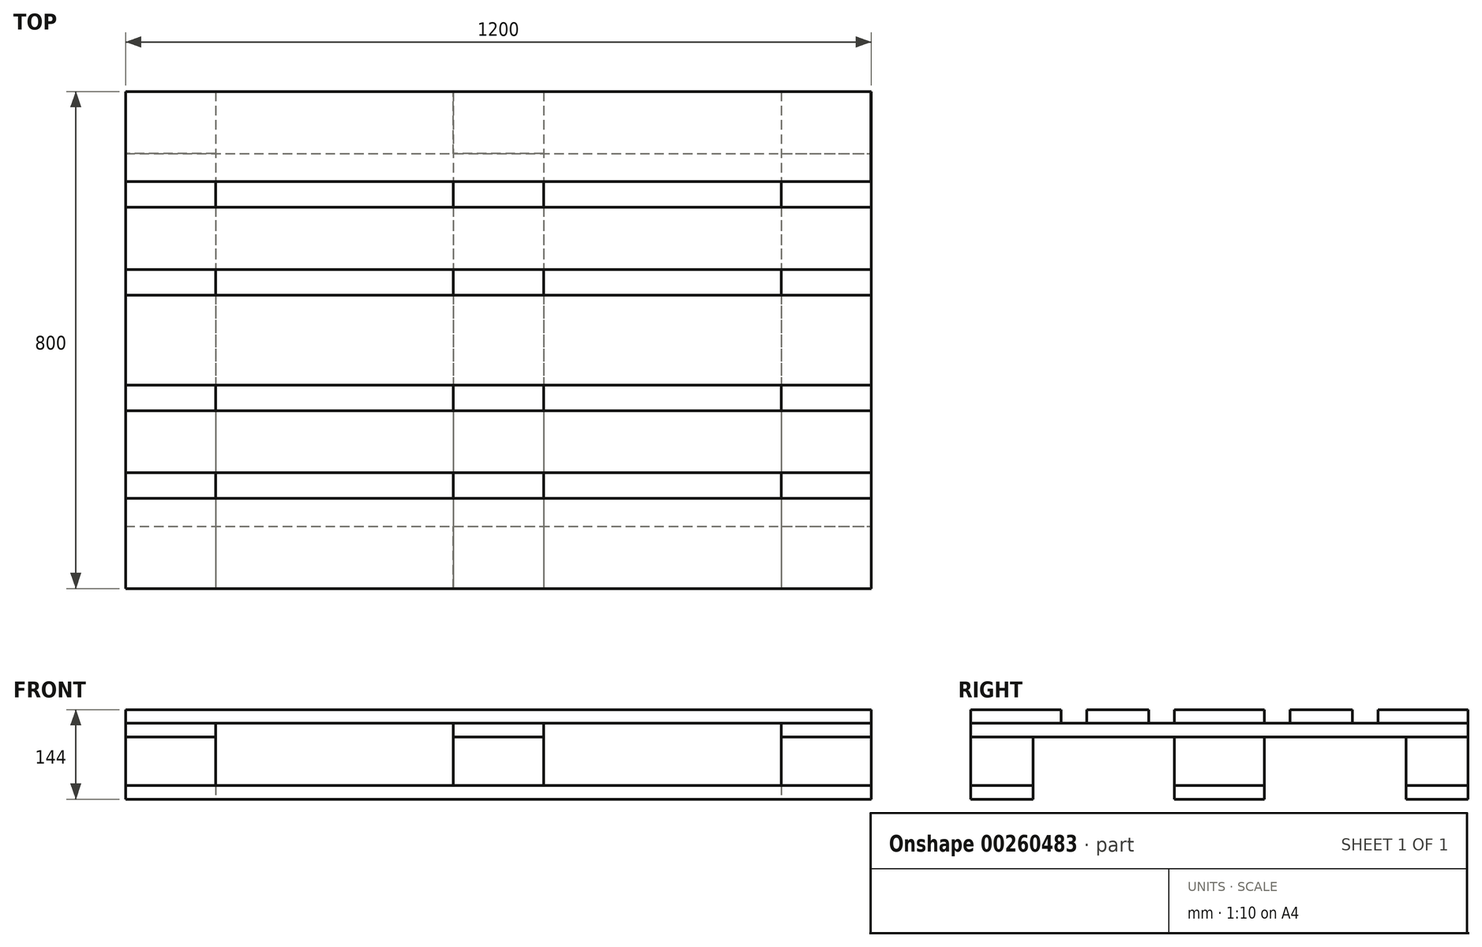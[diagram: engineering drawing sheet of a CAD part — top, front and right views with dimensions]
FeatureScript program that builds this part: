
annotation { "Feature Type Name" : "Feature", "Feature Type Description" : "" }
export const myFeature = defineFeature(function(context is Context, id is Id, definition is map)
    precondition{}
    {
        {
            var Q0;
            Q0=qCreatedBy(makeId("Top.planeOp"),FACE);
            var sketch = newSketch(context, id + "F0", { "sketchPlane" : qUnion([Q0])});
            skLineSegment(sketch, "E0.bottom", {"start": v(0, 800) * mm, "end": v(1200, 800) * mm});
            skLineSegment(sketch, "E0.top", {"start": v(0, 700) * mm, "end": v(1200, 700) * mm});
            skLineSegment(sketch, "E0.left", {"start": v(0, 800) * mm, "end": v(0, 700) * mm});
            skLineSegment(sketch, "E0.right", {"start": v(1200, 800) * mm, "end": v(1200, 700) * mm});
            skLineSegment(sketch, "E1.bottom", {"start": v(0, 100) * mm, "end": v(1200, 100) * mm});
            skLineSegment(sketch, "E1.top", {"start": v(0, 0) * mm, "end": v(1200, 0) * mm});
            skLineSegment(sketch, "E1.left", {"start": v(0, 100) * mm, "end": v(0, 0) * mm});
            skLineSegment(sketch, "E1.right", {"start": v(1200, 100) * mm, "end": v(1200, 0) * mm});
            skLineSegment(sketch, "E2.bottom", {"start": v(0, 472.5) * mm, "end": v(145, 472.5) * mm});
            skLineSegment(sketch, "E2.top", {"start": v(0, 327.5) * mm, "end": v(145, 327.5) * mm});
            skLineSegment(sketch, "E2.left", {"start": v(0, 472.5) * mm, "end": v(0, 327.5) * mm});
            skLineSegment(sketch, "E2.right", {"start": v(145, 472.5) * mm, "end": v(145, 327.5) * mm});
            skLineSegment(sketch, "E3.bottom", {"start": v(1055, 472.5) * mm, "end": v(1200, 472.5) * mm});
            skLineSegment(sketch, "E3.top", {"start": v(1055, 327.5) * mm, "end": v(1200, 327.5) * mm});
            skLineSegment(sketch, "E3.left", {"start": v(1055, 472.5) * mm, "end": v(1055, 327.5) * mm});
            skLineSegment(sketch, "E3.right", {"start": v(1200, 472.5) * mm, "end": v(1200, 327.5) * mm});
            skSolve(sketch);
        }
        {
            var Q0;
            Q0 = qSketchRegion(id + "F0", true);
            extrude(context, id + "F1", {"entities" : qUnion([Q0]), "depth" : 22 * mm});
        }
        {
            var Q0;
            Q0=makeQuery(id+"F1.opExtrude","CAP_FACE",FACE,{"disambiguationData":[OSD([sQuery(id+"F0.wireOp",EDGE,"E1.bottom"),sQuery(id+"F0.wireOp",EDGE,"E1.top"),sQuery(id+"F0.wireOp",EDGE,"E1.left"),sQuery(id+"F0.wireOp",EDGE,"E1.right")])],"isStart":false});
            var sketch = newSketch(context, id + "F2", { "sketchPlane" : qUnion([Q0])});
            skLineSegment(sketch, "E4.0", {"start": v(0, 800) * mm, "end": v(0, 700) * mm});
            skLineSegment(sketch, "E5.0", {"start": v(1200, 800) * mm, "end": v(1200, 700) * mm});
            skLineSegment(sketch, "E6.0", {"start": v(1055, 472.5) * mm, "end": v(1200, 472.5) * mm});
            skLineSegment(sketch, "E7.0.0", {"start": v(1055, 472.5) * mm, "end": v(1055, 327.5) * mm});
            skLineSegment(sketch, "E7.0.1", {"start": v(1055, 327.5) * mm, "end": v(1200, 327.5) * mm});
            skLineSegment(sketch, "E7.0.2", {"start": v(1200, 327.5) * mm, "end": v(1200, 472.5) * mm});
            skLineSegment(sketch, "E7.0.3", {"start": v(1200, 472.5) * mm, "end": v(1055, 472.5) * mm});
            skLineSegment(sketch, "E8.0.0", {"start": v(0, 472.5) * mm, "end": v(0, 327.5) * mm});
            skLineSegment(sketch, "E8.0.1", {"start": v(0, 327.5) * mm, "end": v(145, 327.5) * mm});
            skLineSegment(sketch, "E8.0.2", {"start": v(145, 327.5) * mm, "end": v(145, 472.5) * mm});
            skLineSegment(sketch, "E8.0.3", {"start": v(145, 472.5) * mm, "end": v(0, 472.5) * mm});
            skPoint(sketch, "E9.0", {"position": v(0, 50) * mm});
            skLineSegment(sketch, "E10.0", {"start": v(0, 100) * mm, "end": v(0, 0) * mm});
            skLineSegment(sketch, "E11.0", {"start": v(1200, 100) * mm, "end": v(1200, 0) * mm});
            skLineSegment(sketch, "E12.bottom", {"start": v(0, 800) * mm, "end": v(145, 800) * mm});
            skLineSegment(sketch, "E12.top", {"start": v(0, 800) * mm, "end": v(145, 800) * mm});
            skLineSegment(sketch, "E12.left", {"start": v(0, 800) * mm, "end": v(0, 800) * mm});
            skLineSegment(sketch, "E12.right", {"start": v(145, 800) * mm, "end": v(145, 800) * mm});
            skLineSegment(sketch, "E13.bottom", {"start": v(1200, 800) * mm, "end": v(1055, 800) * mm});
            skLineSegment(sketch, "E13.top", {"start": v(1200, 800) * mm, "end": v(1055, 800) * mm});
            skLineSegment(sketch, "E13.left", {"start": v(1200, 800) * mm, "end": v(1200, 800) * mm});
            skLineSegment(sketch, "E13.right", {"start": v(1055, 800) * mm, "end": v(1055, 800) * mm});
            skLineSegment(sketch, "E14.bottom", {"start": v(1055, 800) * mm, "end": v(1200, 800) * mm});
            skLineSegment(sketch, "E14.top", {"start": v(1055, 700) * mm, "end": v(1200, 700) * mm});
            skLineSegment(sketch, "E14.left", {"start": v(1055, 800) * mm, "end": v(1055, 700) * mm});
            skLineSegment(sketch, "E15.bottom", {"start": v(1200, 100) * mm, "end": v(1055, 100) * mm});
            skLineSegment(sketch, "E15.top", {"start": v(1200, 100) * mm, "end": v(1055, 100) * mm});
            skLineSegment(sketch, "E15.left", {"start": v(1200, 100) * mm, "end": v(1200, 100) * mm});
            skLineSegment(sketch, "E15.right", {"start": v(1055, 100) * mm, "end": v(1055, 100) * mm});
            skLineSegment(sketch, "E16.bottom", {"start": v(1055, 100) * mm, "end": v(1200, 100) * mm});
            skLineSegment(sketch, "E16.top", {"start": v(1055, 0) * mm, "end": v(1200, 0) * mm});
            skLineSegment(sketch, "E16.left", {"start": v(1055, 100) * mm, "end": v(1055, 0) * mm});
            skLineSegment(sketch, "E17.bottom", {"start": v(0, 100) * mm, "end": v(145, 100) * mm});
            skLineSegment(sketch, "E17.top", {"start": v(0, 100) * mm, "end": v(145, 100) * mm});
            skLineSegment(sketch, "E17.left", {"start": v(0, 100) * mm, "end": v(0, 100) * mm});
            skLineSegment(sketch, "E17.right", {"start": v(145, 100) * mm, "end": v(145, 100) * mm});
            skLineSegment(sketch, "E18.bottom", {"start": v(145, 0) * mm, "end": v(0, 0) * mm});
            skLineSegment(sketch, "E18.top", {"start": v(145, 0) * mm, "end": v(0, 0) * mm});
            skLineSegment(sketch, "E18.left", {"start": v(145, 0) * mm, "end": v(145, 0) * mm});
            skLineSegment(sketch, "E18.right", {"start": v(0, 0) * mm, "end": v(0, 0) * mm});
            skLineSegment(sketch, "E19", {"start": v(145, 100) * mm, "end": v(145, 0) * mm});
            skLineSegment(sketch, "E20", {"start": v(145, 800) * mm, "end": v(145, 700) * mm});
            skLineSegment(sketch, "E21", {"start": v(145, 700) * mm, "end": v(0, 700) * mm});
            skLineSegment(sketch, "E22", {"start": v(527.5, 0) * mm, "end": v(527.5, 800) * mm, "construction": true});
            skLineSegment(sketch, "E23", {"start": v(672.5, 800) * mm, "end": v(672.5, 0) * mm, "construction": true});
            skLineSegment(sketch, "E24", {"start": v(527.5, 800) * mm, "end": v(672.5, 800) * mm});
            skLineSegment(sketch, "E25", {"start": v(672.5, 700) * mm, "end": v(527.5, 700) * mm});
            skLineSegment(sketch, "E26", {"start": v(527.5, 700) * mm, "end": v(527.5, 800) * mm});
            skLineSegment(sketch, "E27", {"start": v(527.5, 0) * mm, "end": v(527.5, 100) * mm});
            skLineSegment(sketch, "E28", {"start": v(527.5, 100) * mm, "end": v(672.5, 100) * mm});
            skLineSegment(sketch, "E29", {"start": v(672.5, 100) * mm, "end": v(672.5, 0) * mm});
            skLineSegment(sketch, "E30", {"start": v(527.5, 0) * mm, "end": v(672.5, 0) * mm});
            skLineSegment(sketch, "E31", {"start": v(672.5, 800) * mm, "end": v(672.5, 700) * mm});
            skSolve(sketch);
        }
        {
            var Q0;
            Q0 = qSketchRegion(id + "F2", true);
            extrude(context, id + "F3", {"entities" : qUnion([Q0]), "depth" : 78 * mm});
        }
        {
            var Q0;
            Q0=makeQuery(id+"F3.opExtrude","CAP_FACE",FACE,{"disambiguationData":[OSD([sQuery(id+"F2.wireOp",EDGE,"E10.0"),sQuery(id+"F2.wireOp",EDGE,"E17.top"),sQuery(id+"F2.wireOp",EDGE,"E18.top"),sQuery(id+"F2.wireOp",EDGE,"E19")])],"isStart":false});
            var sketch = newSketch(context, id + "F4", { "sketchPlane" : qUnion([Q0])});
            skPoint(sketch, "E32.0", {"position": v(0, 800) * mm});
            skPoint(sketch, "E33.0", {"position": v(145, 0) * mm});
            skPoint(sketch, "E34.0", {"position": v(527.5, 800) * mm});
            skPoint(sketch, "E35.0", {"position": v(672.5, 0) * mm});
            skPoint(sketch, "E36.0", {"position": v(1055, 800) * mm});
            skPoint(sketch, "E37.0", {"position": v(1200, 0) * mm});
            skLineSegment(sketch, "E38.bottom", {"start": v(0, 800) * mm, "end": v(145, 800) * mm});
            skLineSegment(sketch, "E38.top", {"start": v(0, 0) * mm, "end": v(145, 0) * mm});
            skLineSegment(sketch, "E38.left", {"start": v(0, 800) * mm, "end": v(0, 0) * mm});
            skLineSegment(sketch, "E38.right", {"start": v(145, 800) * mm, "end": v(145, 0) * mm});
            skLineSegment(sketch, "E39.bottom", {"start": v(527.5, 800) * mm, "end": v(672.5, 800) * mm});
            skLineSegment(sketch, "E39.top", {"start": v(527.5, 0) * mm, "end": v(672.5, 0) * mm});
            skLineSegment(sketch, "E39.left", {"start": v(527.5, 800) * mm, "end": v(527.5, 0) * mm});
            skLineSegment(sketch, "E39.right", {"start": v(672.5, 800) * mm, "end": v(672.5, 0) * mm});
            skLineSegment(sketch, "E40.bottom", {"start": v(1055, 800) * mm, "end": v(1200, 800) * mm});
            skLineSegment(sketch, "E40.top", {"start": v(1055, 0) * mm, "end": v(1200, 0) * mm});
            skLineSegment(sketch, "E40.left", {"start": v(1055, 800) * mm, "end": v(1055, 0) * mm});
            skLineSegment(sketch, "E40.right", {"start": v(1200, 800) * mm, "end": v(1200, 0) * mm});
            skSolve(sketch);
        }
        {
            var Q0;
            Q0 = qSketchRegion(id + "F4", true);
            extrude(context, id + "F5", {"entities" : qUnion([Q0]), "depth" : 22 * mm});
        }
        {
            var Q0;
            Q0=makeQuery(id+"F5.opExtrude","CAP_FACE",FACE,{"disambiguationData":[OSD([sQuery(id+"F4.wireOp",EDGE,"E38.bottom"),sQuery(id+"F4.wireOp",EDGE,"E38.top"),sQuery(id+"F4.wireOp",EDGE,"E38.left"),sQuery(id+"F4.wireOp",EDGE,"E38.right")])],"isStart":false});
            var sketch = newSketch(context, id + "F6", { "sketchPlane" : qUnion([Q0])});
            skLineSegment(sketch, "E41.bottom", {"start": v(0, 0) * mm, "end": v(1200, 0) * mm});
            skLineSegment(sketch, "E41.top", {"start": v(0, 145) * mm, "end": v(1200, 145) * mm});
            skLineSegment(sketch, "E41.left", {"start": v(0, 0) * mm, "end": v(0, 145) * mm});
            skLineSegment(sketch, "E41.right", {"start": v(1200, 0) * mm, "end": v(1200, 145) * mm});
            skLineSegment(sketch, "E42.bottom", {"start": v(0, 800) * mm, "end": v(1199.38, 800) * mm});
            skLineSegment(sketch, "E42.top", {"start": v(0, 655) * mm, "end": v(1199.38, 655) * mm});
            skLineSegment(sketch, "E42.left", {"start": v(0, 800) * mm, "end": v(0, 655) * mm});
            skLineSegment(sketch, "E42.right", {"start": v(1199.38, 800) * mm, "end": v(1199.38, 655) * mm});
            skLineSegment(sketch, "E43.bottom", {"start": v(0, 613.75) * mm, "end": v(1200, 613.75) * mm});
            skLineSegment(sketch, "E43.top", {"start": v(0, 513.75) * mm, "end": v(1200, 513.75) * mm});
            skLineSegment(sketch, "E43.left", {"start": v(0, 613.75) * mm, "end": v(0, 513.75) * mm});
            skLineSegment(sketch, "E43.right", {"start": v(1200, 613.75) * mm, "end": v(1200, 513.75) * mm});
            skLineSegment(sketch, "E44.bottom", {"start": v(0, 472.5) * mm, "end": v(1200, 472.5) * mm});
            skLineSegment(sketch, "E44.top", {"start": v(0, 327.5) * mm, "end": v(1200, 327.5) * mm});
            skLineSegment(sketch, "E44.left", {"start": v(0, 472.5) * mm, "end": v(0, 327.5) * mm});
            skLineSegment(sketch, "E44.right", {"start": v(1200, 472.5) * mm, "end": v(1200, 327.5) * mm});
            skLineSegment(sketch, "E45.bottom", {"start": v(0, 286.25) * mm, "end": v(1200, 286.25) * mm});
            skLineSegment(sketch, "E45.top", {"start": v(0, 186.25) * mm, "end": v(1200, 186.25) * mm});
            skLineSegment(sketch, "E45.left", {"start": v(0, 286.25) * mm, "end": v(0, 186.25) * mm});
            skLineSegment(sketch, "E45.right", {"start": v(1200, 286.25) * mm, "end": v(1200, 186.25) * mm});
            skLineSegment(sketch, "E46", {"start": v(0, 0) * mm, "end": v(0, 800) * mm, "construction": true});
            skLineSegment(sketch, "E47.0", {"start": v(1200, 800) * mm, "end": v(1200, 0) * mm, "construction": true});
            skSolve(sketch);
        }
        {
            var Q0;
            Q0 = qSketchRegion(id + "F6", true);
            extrude(context, id + "F7", {"entities" : qUnion([Q0]), "depth" : 22 * mm});
        }
    });
